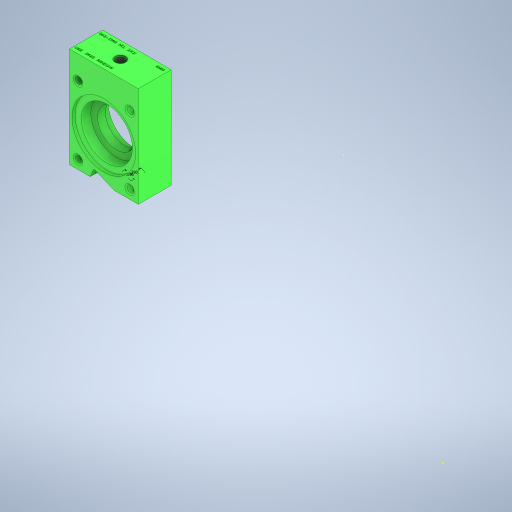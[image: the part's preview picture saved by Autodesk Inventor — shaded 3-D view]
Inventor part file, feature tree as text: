
AUTODESK INVENTOR PART (.ipt)
format: ipt  version: 2024.1 (Build 281209000, 209)  size: 1,137,664 bytes
history: native  units: in
note: dims shown in document units (in); Inventor stores cm internally (conversion verified against a paired STEP export)
features: hole x7, extrude x4, sketch x4, fillet x1
ambient origin geometry x8: Origin, YZ Plane, XZ Plane, XY Plane, X Axis, Y Axis, Z Axis, Center Point
bodies: Solid1 (feature_tree)
feature tree (16):
  extrude  "Extrusion1"  Depth=0.4in TaperAngle=0.0deg
  extrude  "Extrusion2"  Depth=0.0312in
  extrude  "Extrusion3"  Depth=0.0312in
  hole  "Hole1"  [1 undecoded]
  hole  "Hole2"  [1 undecoded]
  extrude  "Extrusion4"  Depth=0.0312in
  hole  "Hole5"  [1 undecoded]
  hole  "Hole6"  [1 undecoded]
  fillet  "Fillet1"  Radius=1.0in
  hole  "Hole7"  [1 undecoded]
  hole  "Hole3"  [1 undecoded]
  hole  "Hole4"  [1 undecoded]
  sketch  "Sketch1"  dims[d0=0.5in d1=0.0in d2=0.4in d3=0.0in]
  sketch  "Sketch2"  dims[d4=0.6in d5=0.0in]
  sketch  "Sketch5"  dims[d6=0.211in d7=0.25in d8=0.507in d9=0.25in d10=0.5635in d11=0.25in d12=0.0in]
  sketch  "Sketch7"  dims[d13=0.06in d14=0.75in d15=0.507in d16=0.25in d17=0.5635in d18=1.0in d19=0.8108in d20=0.4583in d21=0.29in d22=0.04in d23=0.75in d24=0.507in d25=0.25in d26=0.5635in d27=1.0in d28=0.8108in d29=0.213in d30=0.75in d31=0.507in d32=0.25in d33=0.5635in d34=0.25in d35=0.0in d36=0.75in d38=135.0deg d39=0.4583in d40=112.5deg d41=0.25in d42=1.0in d43=0.0in d44=0.29in d45=0.196in d46=0.211in d47=0.22in d48=0.375in d49=0.25in d50=0.5635in d51=0.22in d52=0.0in d53=0.06in d54=0.75in d55=0.375in d56=0.25in d57=0.5635in d58=0.6in d59=0.8108in d60=0.0312in d61=0.13in d62=1.0in d63=0.375in d64=0.25in d65=0.5635in d66=0.484in d67=0.8108in]
note: 7 required parameter values undecoded (feature->parameter linkage not recoverable at this tier; creation-order binding heuristic only, values carry confidence <= 0.55)
